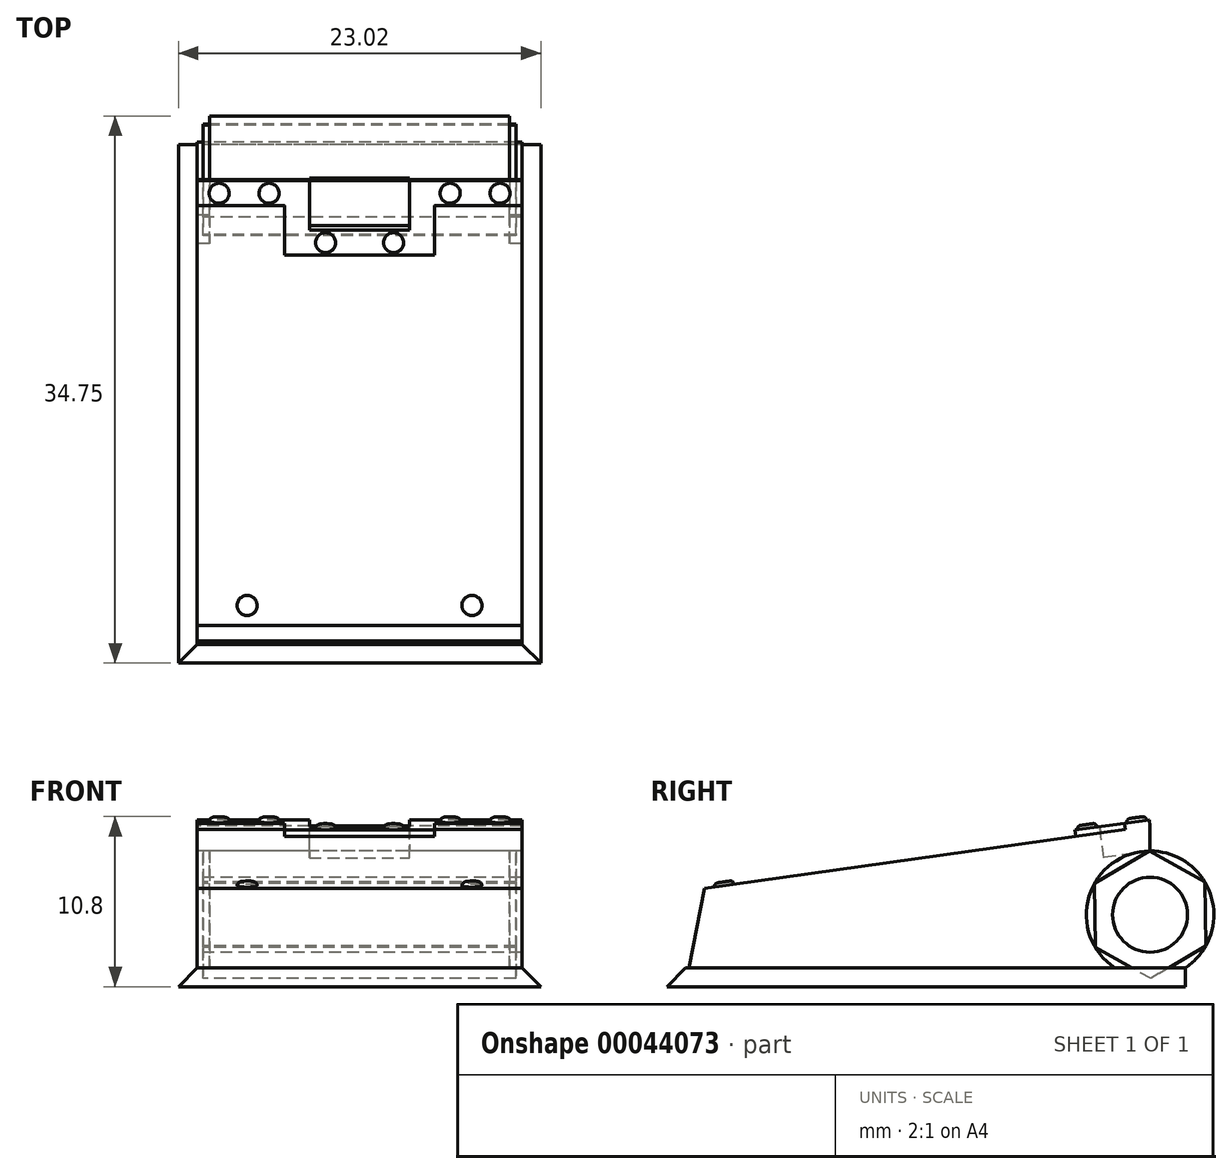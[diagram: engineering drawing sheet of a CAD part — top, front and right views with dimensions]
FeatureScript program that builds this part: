
annotation { "Feature Type Name" : "Feature", "Feature Type Description" : "" }
export const myFeature = defineFeature(function(context is Context, id is Id, definition is map)
    precondition{}
    {
        {
            var Q0;
            Q0=qCreatedBy(makeId("Right.planeOp"),FACE);
            var sketch = newSketch(context, id + "F0", { "sketchPlane" : qUnion([Q0])});
            skLineSegment(sketch, "E0", {"start": v(0, 0) * mm, "end": v(-31.75, 0) * mm});
            skLineSegment(sketch, "E1", {"start": v(-31.75, 0) * mm, "end": v(-30.54, 6.23) * mm});
            skLineSegment(sketch, "E2", {"start": v(-30.54, 6.23) * mm, "end": v(-2.24, 10.21) * mm});
            skCircle(sketch, "E3", {"center": v(-2.24, 4.57) * mm, "radius": 4.05 * mm});
            skLineSegment(sketch, "E4", {"start": v(-2.24, 10.21) * mm, "end": v(-2.24, 8.62) * mm});
            skLineSegment(sketch, "E5", {"start": v(0, 0) * mm, "end": v(0, 1.2) * mm});
            skSolve(sketch);
        }
        {
            var Q0;
            Q0=makeQuery(id+"F0.imprint","IMPRINT",FACE,{"disambiguationData":[TD([[makeQuery(id+"F0.imprint","IMPRINT",EDGE,{"derivedFrom":sQuery(id+"F0.wireOp",EDGE,"E0")}),-1.0]])]});
            extrude(context, id + "F1", {"entities" : qUnion([Q0]), "endBound" : BoundingType.SYMMETRIC, "depth" : 20.64 * mm});
        }
        {
            var Q0;
            Q0=qCreatedBy(makeId("Right.planeOp"),FACE);
            var sketch = newSketch(context, id + "F2", { "sketchPlane" : qUnion([Q0])});
            skCircle(sketch, "E6", {"center": v(-2.24, 4.57) * mm, "radius": 4.05 * mm});
            skSolve(sketch);
        }
        {
            var Q0;
            Q0=qSketchRegion(id+"F2",true);
            extrude(context, id + "F3", {"entities" : qUnion([Q0]), "endBound" : BoundingType.SYMMETRIC, "depth" : 19.05 * mm});
        }
        {
            var Q0;
            Q0=makeQuery(id+"F1.opExtrude","SWEPT_FACE",FACE,{"disambiguationData":[OSD([sQuery(id+"F0.wireOp",EDGE,"E2")])]});
            var sketch = newSketch(context, id + "F4", { "sketchPlane" : qUnion([Q0])});
            skLineSegment(sketch, "E7", {"start": v(0, -0.8) * mm, "end": v(-3.18, -0.8) * mm});
            skLineSegment(sketch, "E8", {"start": v(-3.18, -0.8) * mm, "end": v(-3.18, -3.97) * mm});
            skLineSegment(sketch, "E9", {"start": v(-3.18, -3.97) * mm, "end": v(3.18, -3.97) * mm});
            skLineSegment(sketch, "E10", {"start": v(3.17, -3.97) * mm, "end": v(3.17, -0.8) * mm});
            skLineSegment(sketch, "E11", {"start": v(3.17, -0.8) * mm, "end": v(0, -0.8) * mm});
            skSolve(sketch);
        }
        {
            var Q0;
            Q0=qSketchRegion(id+"F4",true);
            extrude(context, id + "F5", {"entities" : qUnion([Q0]), "operationType" : NewBodyOperationType.REMOVE, "oppositeDirection" : true, "depth" : 1.59 * mm});
        }
        {
            var Q0;
            Q0=makeQuery(id+"F1.opExtrude","SWEPT_FACE",FACE,{"disambiguationData":[OSD([sQuery(id+"F0.wireOp",EDGE,"E5")])]});
            var sketch = newSketch(context, id + "F6", { "sketchPlane" : qUnion([Q0])});
            skLineSegment(sketch, "E12", {"start": v(0, 0) * mm, "end": v(-11.51, 0) * mm});
            skLineSegment(sketch, "E13", {"start": v(11.51, 0) * mm, "end": v(0, 0) * mm});
            skLineSegment(sketch, "E14", {"start": v(0, 0) * mm, "end": v(0, 1.2) * mm});
            skLineSegment(sketch, "E15", {"start": v(-11.51, 0) * mm, "end": v(-11.51, 1.2) * mm});
            skLineSegment(sketch, "E16", {"start": v(-11.51, 1.2) * mm, "end": v(11.51, 1.2) * mm});
            skLineSegment(sketch, "E17", {"start": v(11.51, 1.2) * mm, "end": v(11.51, 0) * mm});
            skSolve(sketch);
        }
        {
            var Q0;
            Q0=qSketchRegion(id+"F6",true);
            extrude(context, id + "F7", {"entities" : qUnion([Q0]), "operationType" : NewBodyOperationType.ADD, "oppositeDirection" : true, "depth" : 32.94 * mm});
        }
        {
            var Q0;
            Q0=makeQuery(id+"F7.opExtrude","SWEPT_EDGE",EDGE,{"disambiguationData":[OSD([sQuery(id+"F6.wireOp",EDGE,"E15"),sQuery(id+"F6.wireOp",EDGE,"E16")])]});
            var Q1;
            Q1=makeQuery(id+"F7.opExtrude","CAP_EDGE",EDGE,{"disambiguationData":[OSD([sQuery(id+"F6.wireOp",EDGE,"E16")])],"isStart":false});
            var Q2;
            Q2=makeQuery(id+"F7.opExtrude","SWEPT_EDGE",EDGE,{"disambiguationData":[OSD([sQuery(id+"F6.wireOp",EDGE,"E16"),sQuery(id+"F6.wireOp",EDGE,"E17")])]});
            chamfer(context, id + "F8", {"entities" : qUnion([Q0, Q1, Q2]), "width" : 1.2 * mm, "tangentPropagation" : true});
        }
        {
            var Q0;
            Q0=makeQuery(id+"F3.opExtrude","CAP_FACE",FACE,{"disambiguationData":[OSD([sQuery(id+"F2.wireOp",EDGE,"E6")])],"isStart":false});
            var sketch = newSketch(context, id + "F9", { "sketchPlane" : qUnion([Q0])});
            skCircle(sketch, "E18.cCircle", {"center": v(-2.24, 4.57) * mm, "radius": 4.05 * mm, "construction": true});
            skLineSegment(sketch, "E18.0", {"start": v(-2.29, 8.62) * mm, "end": v(1.24, 6.64) * mm});
            skLineSegment(sketch, "E18.1", {"start": v(1.24, 6.64) * mm, "end": v(1.3, 2.59) * mm});
            skLineSegment(sketch, "E18.2", {"start": v(1.3, 2.59) * mm, "end": v(-2.2, 0.52) * mm});
            skLineSegment(sketch, "E18.3", {"start": v(-2.2, 0.52) * mm, "end": v(-5.73, 2.5) * mm});
            skLineSegment(sketch, "E18.4", {"start": v(-5.73, 2.5) * mm, "end": v(-5.77, 6.55) * mm});
            skLineSegment(sketch, "E18.5", {"start": v(-5.77, 6.55) * mm, "end": v(-2.29, 8.62) * mm});
            skSolve(sketch);
        }
        {
            var Q0;
            Q0=qSketchRegion(id+"F9",true);
            extrude(context, id + "F10", {"entities" : qUnion([Q0]), "depth" : 0.4 * mm, "hasSecondDirection" : true, "secondDirectionOppositeDirection" : true, "secondDirectionDepth" : 19.45 * mm});
        }
        {
            var Q0;
            Q0=makeQuery(id+"F10.opExtrude","CAP_FACE",FACE,{"disambiguationData":[OSD([sQuery(id+"F9.wireOp",EDGE,"E18.0"),sQuery(id+"F9.wireOp",EDGE,"E18.1"),sQuery(id+"F9.wireOp",EDGE,"E18.2"),sQuery(id+"F9.wireOp",EDGE,"E18.3"),sQuery(id+"F9.wireOp",EDGE,"E18.4"),sQuery(id+"F9.wireOp",EDGE,"E18.5")])],"isStart":false});
            var sketch = newSketch(context, id + "F11", { "sketchPlane" : qUnion([Q0])});
            skSolve(sketch);
        }
        {
            var Q0;
            Q0=makeQuery(id+"F11.imprint","IMPRINT",FACE,{"disambiguationData":[TD([[makeQuery(id+"F11.imprint","IMPRINT",EDGE,{"derivedFrom":makeQuery(id+"F10.opExtrude","CAP_EDGE",EDGE,{"disambiguationData":[OSD([sQuery(id+"F9.wireOp",EDGE,"E18.0")])],"isStart":false})}),-1.0]])]});
            var sketch = newSketch(context, id + "F12", { "sketchPlane" : qUnion([Q0])});
            skCircle(sketch, "E19", {"center": v(-2.24, 4.57) * mm, "radius": 2.38 * mm});
            skSolve(sketch);
        }
        {
            var Q0;
            Q0=qSketchRegion(id+"F12",true);
            extrude(context, id + "F13", {"entities" : qUnion([Q0]), "depth" : 0.4 * mm, "hasSecondDirection" : true, "secondDirectionOppositeDirection" : true, "secondDirectionDepth" : 20.24 * mm});
        }
        {
            var Q0;
            Q0=makeQuery(id+"F1.opExtrude","SWEPT_FACE",FACE,{"disambiguationData":[OSD([sQuery(id+"F0.wireOp",EDGE,"E2")])]});
            var sketch = newSketch(context, id + "F14", { "sketchPlane" : qUnion([Q0])});
            skLineSegment(sketch, "E20", {"start": v(-10.32, -0.8) * mm, "end": v(-10.32, -2.39) * mm});
            skLineSegment(sketch, "E21", {"start": v(-10.32, -2.39) * mm, "end": v(-4.76, -2.39) * mm});
            skLineSegment(sketch, "E22", {"start": v(-4.76, -2.39) * mm, "end": v(-4.76, -5.56) * mm});
            skLineSegment(sketch, "E23", {"start": v(-4.76, -5.56) * mm, "end": v(4.76, -5.56) * mm});
            skLineSegment(sketch, "E24", {"start": v(4.76, -5.56) * mm, "end": v(4.76, -2.39) * mm});
            skLineSegment(sketch, "E25", {"start": v(4.76, -2.39) * mm, "end": v(10.32, -2.39) * mm});
            skLineSegment(sketch, "E26", {"start": v(10.32, -2.39) * mm, "end": v(10.32, -0.8) * mm});
            skLineSegment(sketch, "E27", {"start": v(10.32, -0.8) * mm, "end": v(3.18, -0.8) * mm});
            skLineSegment(sketch, "E28", {"start": v(3.18, -0.8) * mm, "end": v(3.18, -3.97) * mm});
            skLineSegment(sketch, "E29", {"start": v(3.18, -3.97) * mm, "end": v(-3.18, -3.97) * mm});
            skLineSegment(sketch, "E30", {"start": v(-3.18, -3.97) * mm, "end": v(-3.18, -0.8) * mm});
            skLineSegment(sketch, "E31", {"start": v(-3.18, -0.8) * mm, "end": v(-10.32, -0.8) * mm});
            skSolve(sketch);
        }
        {
            var Q0;
            Q0=qSketchRegion(id+"F14",true);
            extrude(context, id + "F15", {"entities" : qUnion([Q0]), "operationType" : NewBodyOperationType.ADD, "depth" : 0.4 * mm});
        }
        {
            var Q0;
            Q0=makeQuery(id+"F1.opExtrude","SWEPT_FACE",FACE,{"disambiguationData":[OSD([sQuery(id+"F0.wireOp",EDGE,"E2")])]});
            var sketch = newSketch(context, id + "F16", { "sketchPlane" : qUnion([Q0])});
            skCircle(sketch, "E32", {"center": v(-7.14, -28.1) * mm, "radius": 0.64 * mm});
            skCircle(sketch, "E33", {"center": v(7.14, -28.1) * mm, "radius": 0.64 * mm});
            skSolve(sketch);
        }
        {
            var Q0;
            Q0=qSketchRegion(id+"F16",true);
            extrude(context, id + "F17", {"entities" : qUnion([Q0]), "operationType" : NewBodyOperationType.ADD, "depth" : 0.25 * mm});
        }
        {
            var Q0;
            Q0=makeQuery(id+"F17.opExtrude","CAP_EDGE",EDGE,{"disambiguationData":[OSD([sQuery(id+"F16.wireOp",EDGE,"E32")])],"isStart":false});
            var Q1;
            Q1=makeQuery(id+"F17.opExtrude","CAP_FACE",FACE,{"disambiguationData":[OSD([sQuery(id+"F16.wireOp",EDGE,"E33")])],"isStart":false});
            fillet(context, id + "F18", {"entities" : qUnion([Q0, Q1]), "radius" : 0.25 * mm, "tangentPropagation" : true, "allowEdgeOverflow" : false});
        }
        {
            var Q0;
            Q0=makeQuery(id+"F15.opExtrude","CAP_FACE",FACE,{"disambiguationData":[OSD([sQuery(id+"F14.wireOp",EDGE,"E20"),sQuery(id+"F14.wireOp",EDGE,"E21"),sQuery(id+"F14.wireOp",EDGE,"E22"),sQuery(id+"F14.wireOp",EDGE,"E23"),sQuery(id+"F14.wireOp",EDGE,"E24"),sQuery(id+"F14.wireOp",EDGE,"E25"),sQuery(id+"F14.wireOp",EDGE,"E26"),sQuery(id+"F14.wireOp",EDGE,"E27"),sQuery(id+"F14.wireOp",EDGE,"E28"),sQuery(id+"F14.wireOp",EDGE,"E29"),sQuery(id+"F14.wireOp",EDGE,"E30"),sQuery(id+"F14.wireOp",EDGE,"E31")])],"isStart":false});
            var sketch = newSketch(context, id + "F19", { "sketchPlane" : qUnion([Q0])});
            skCircle(sketch, "E34", {"center": v(-8.92, -1.6) * mm, "radius": 0.64 * mm});
            skCircle(sketch, "E35", {"center": v(-5.75, -1.6) * mm, "radius": 0.64 * mm});
            skCircle(sketch, "E36", {"center": v(-2.16, -4.77) * mm, "radius": 0.64 * mm});
            skCircle(sketch, "E37", {"center": v(2.16, -4.77) * mm, "radius": 0.64 * mm});
            skCircle(sketch, "E38", {"center": v(5.75, -1.6) * mm, "radius": 0.64 * mm});
            skCircle(sketch, "E39", {"center": v(8.92, -1.6) * mm, "radius": 0.64 * mm});
            skSolve(sketch);
        }
        {
            var Q0;
            Q0=qSketchRegion(id+"F19",true);
            extrude(context, id + "F20", {"entities" : qUnion([Q0]), "operationType" : NewBodyOperationType.ADD, "depth" : 0.25 * mm});
        }
        {
            var Q0;
            Q0=makeQuery(id+"F20.opExtrude","CAP_EDGE",EDGE,{"disambiguationData":[OSD([sQuery(id+"F19.wireOp",EDGE,"E34")])],"isStart":false});
            var Q1;
            Q1=makeQuery(id+"F20.opExtrude","CAP_EDGE",EDGE,{"disambiguationData":[OSD([sQuery(id+"F19.wireOp",EDGE,"E35")])],"isStart":false});
            var Q2;
            Q2=makeQuery(id+"F20.opExtrude","CAP_EDGE",EDGE,{"disambiguationData":[OSD([sQuery(id+"F19.wireOp",EDGE,"E36")])],"isStart":false});
            var Q3;
            Q3=makeQuery(id+"F20.opExtrude","CAP_FACE",FACE,{"disambiguationData":[OSD([sQuery(id+"F19.wireOp",EDGE,"E37")])],"isStart":false});
            var Q4;
            Q4=makeQuery(id+"F20.opExtrude","CAP_FACE",FACE,{"disambiguationData":[OSD([sQuery(id+"F19.wireOp",EDGE,"E38")])],"isStart":false});
            var Q5;
            Q5=makeQuery(id+"F20.opExtrude","CAP_FACE",FACE,{"disambiguationData":[OSD([sQuery(id+"F19.wireOp",EDGE,"E39")])],"isStart":false});
            fillet(context, id + "F21", {"entities" : qUnion([Q0, Q1, Q2, Q3, Q4, Q5]), "radius" : 0.25 * mm, "tangentPropagation" : true, "allowEdgeOverflow" : false});
        }
    });
